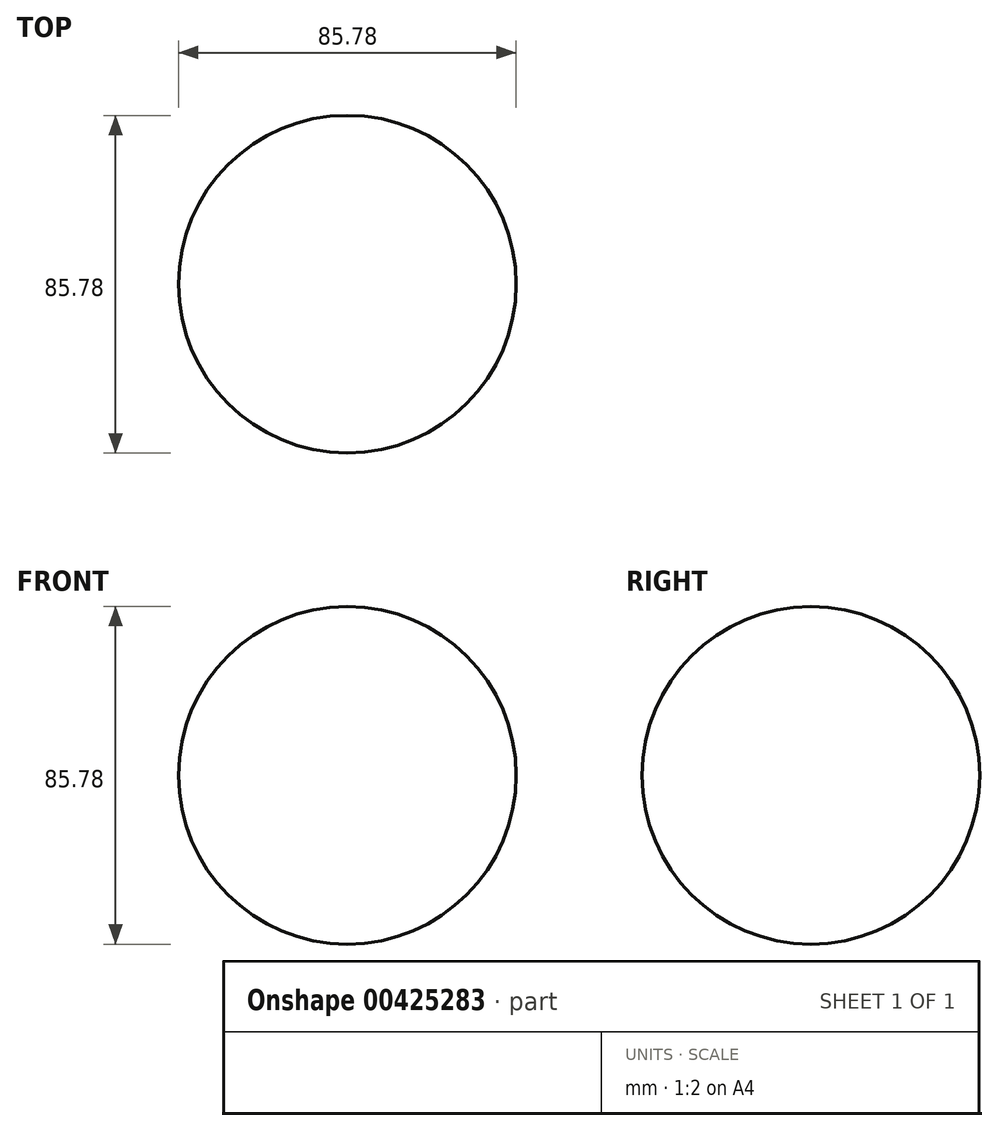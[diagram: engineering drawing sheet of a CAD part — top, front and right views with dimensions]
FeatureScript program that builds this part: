
annotation { "Feature Type Name" : "Feature", "Feature Type Description" : "" }
export const myFeature = defineFeature(function(context is Context, id is Id, definition is map)
    precondition{}
    {
        {
            var Q0;
            Q0=qCreatedBy(makeId("Front.planeOp"),FACE);
            var sketch = newSketch(context, id + "F0", { "sketchPlane" : qUnion([Q0])});
            skArc(sketch, "E0", {"start": v(0, 42.7) * mm, "mid": v(-42.9, -0.2) * mm, "end": v(0, -43.08) * mm});
            skPoint(sketch, "E1.orphan", {"position": v(0, 47.17) * mm});
            skLineSegment(sketch, "E2", {"start": v(0, 42.7) * mm, "end": v(0, -43.08) * mm});
            skSolve(sketch);
        }
        {
            var Q0;
            Q0=makeQuery(id+"F0.imprint","IMPRINT",FACE,{"disambiguationData":[TD([[makeQuery(id+"F0.imprint","IMPRINT",EDGE,{"derivedFrom":sQuery(id+"F0.wireOp",EDGE,"E0")}),1.0]])]});
            var Q1;
            Q1=sQuery(id+"F0.wireOp",EDGE,"E2");
            revolve(context, id + "F1", {"entities" : qUnion([Q0]), "axis" : qUnion([Q1]), "revolveType" : RevolveType.FULL});
        }
    });
